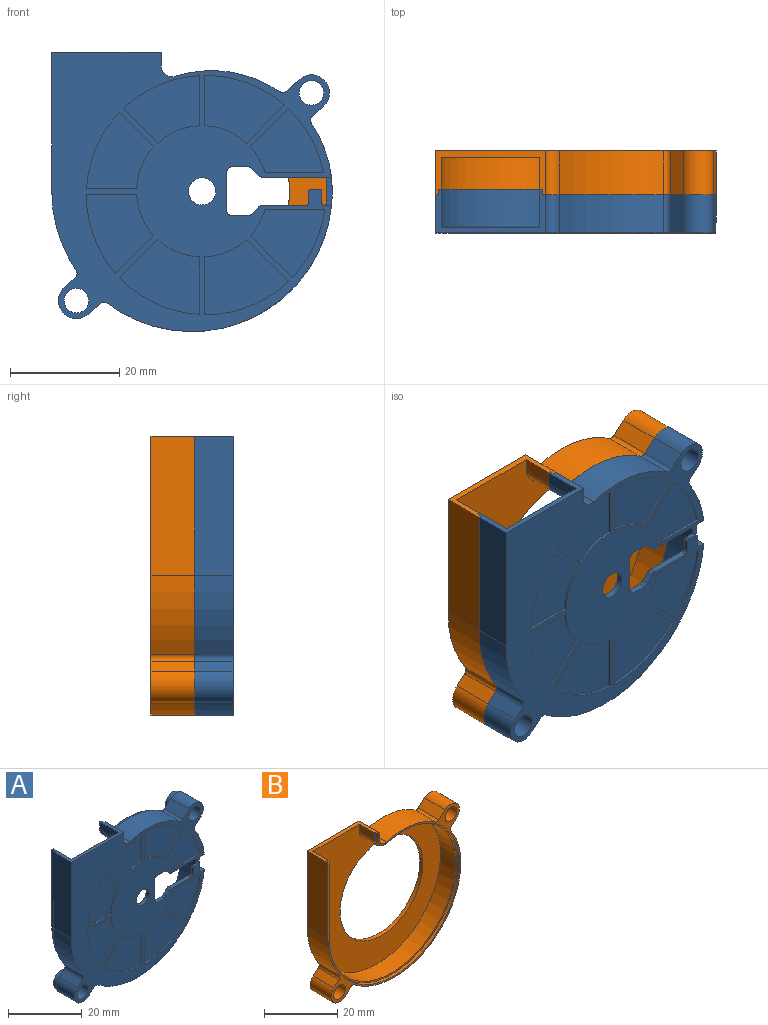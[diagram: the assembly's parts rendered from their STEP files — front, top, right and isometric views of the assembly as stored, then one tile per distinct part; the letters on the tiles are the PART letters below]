
ASSEMBLY  parts=2 mates=1
PART A: 104 faces, bbox 52.9x8.5x51.4 mm
  f0: torus R=1.41mm, axis (0,-1,0), area 1.6mm2, adj f31,f35,f102,f103
  f1: cylinder r=21.88mm len=15.3mm, axis (0,-1,0), area 8.4mm2, adj f14,f53,f54,f55
  f2: cylinder r=2.82mm len=5.65mm, axis (0,-1,0), area 26.6mm2, adj f15,f41
  f3: cylinder r=2.82mm len=5.65mm, axis (0,-1,0), area 26.6mm2, adj f15,f40
  f4: cylinder r=21.57mm len=28.05mm, axis (0,1,0), area 40.5mm2, adj f15,f16,f37,f38
  f5: cylinder r=21.07mm len=27.4mm, axis (0,1,0), area 266.7mm2, adj f16,f31,f33,f34,f86,f87
  f6: cylinder r=2.5mm len=5mm, axis (0,-1,0), area 18.8mm2, adj f14,f31
  f7: cylinder r=2.25mm len=8.5mm, axis (0,-1,0), area 120.2mm2, adj f14,f40
  f8: cylinder r=2.25mm len=8.5mm, axis (0,-1,0), area 120.2mm2, adj f14,f41
  f9: cylinder r=25.65mm len=41.13mm, axis (0,-1,0), area 393.3mm2, adj f13,f14,f15,f28,f29,f87
  f10: cylinder r=1mm len=7mm, axis (0,-1,0), area 9.3mm2, adj f14,f15,f23,f24
  f11: cylinder r=2mm len=7mm, axis (0,-1,0), area 26.3mm2, adj f14,f15,f22,f23
  f12: cylinder r=3.3mm len=7mm, axis (0,-1,0), area 72.6mm2, adj f14,f15,f17,f30
  f13: plane 12.66x2mm, normal (0,0,1), area 13.2mm2, adj f9,f14,f31,f34,f87,f93,f95,f98
  f14: plane 51.17x51.07mm, normal (0,-1,0), area 1131.7mm2, adj f1,f6,f7,f8,f9,f10,f11,f12
  f15: plane 51.3x51.07mm, normal (0,1,0), area 108.5mm2, adj f2,f3,f4,f9,f10,f11,f12,f17
  f16: plane 50.57x50.3mm, normal (0,1,0), area 75.6mm2, adj f4,f5,f21,f32,f33,f34,f35,f36
  f17: plane 7x1.98mm, normal (-0.66,0,0.75), area 18.5mm2, adj f12,f14,f15,f18
  f18: cylinder r=1mm len=7mm, axis (0,-1,0), area 10.1mm2, adj f14,f15,f17,f19
  f19: cylinder r=25.65mm len=14.47mm, axis (0,-1,0), area 107.6mm2, adj f14,f15,f18,f20
  f20: plane 25.4x7mm, normal (-1,0,0), area 177.8mm2, adj f14,f15,f19,f21
  f21: plane 20x8mm, normal (0,0,1), area 31.2mm2, adj f14,f15,f16,f20,f22,f32,f35,f36
  f22: plane 7x2.44mm, normal (1,0,0), area 17.1mm2, adj f11,f14,f15,f21
  f23: cylinder r=22.07mm len=19.05mm, axis (0,-1,0), area 139.5mm2, adj f10,f11,f14,f15
  f24: plane 7x2.44mm, normal (-0.66,0,0.75), area 22.8mm2, adj f10,f14,f15,f25
  f25: cylinder r=3.3mm len=7mm, axis (0,-1,0), area 72.6mm2, adj f14,f15,f24,f26
  f26: plane 7x2.04mm, normal (0.66,0,-0.75), area 19.1mm2, adj f14,f15,f25,f27
  f27: cylinder r=1mm len=7mm, axis (0,-1,0), area 10.1mm2, adj f14,f15,f26,f28
  f28: cylinder r=22.07mm len=12.41mm, axis (0,-1,0), area 87.1mm2, adj f9,f14,f15,f27,f86,f87
  f29: cylinder r=1mm len=7mm, axis (0,-1,0), area 9.6mm2, adj f9,f14,f15,f30
  f30: plane 7x2.22mm, normal (0.66,0,-0.75), area 20.7mm2, adj f12,f14,f15,f29
  f31: plane 49.16x46.35mm, normal (0,1,0), area 1650.7mm2, adj f0,f5,f6,f13,f33,f34,f35,f81
  f32: plane 7.1x2.44mm, normal (-1,0,0), area 17.4mm2, adj f16,f21,f33,f102
  f33: cylinder r=3mm len=7.1mm, axis (0,1,0), area 38.5mm2, adj f5,f16,f31,f32,f103
  f34: cylinder r=24.65mm len=49.3mm, axis (0,1,0), area 524.7mm2, adj f5,f13,f16,f31,f35,f87
  f35: plane 25.4x7.1mm, normal (1,0,0), area 179.6mm2, adj f0,f16,f21,f31,f34,f102
  f36: plane 25.4x1mm, normal (-1,0,0), area 25.4mm2, adj f15,f16,f21,f37
  f37: cylinder r=25.15mm len=50.3mm, axis (0,1,0), area 79mm2, adj f4,f15,f16,f36
  f38: cylinder r=2.5mm len=3.25mm, axis (0,1,0), area 4.7mm2, adj f4,f15,f16,f39
  f39: plane 2.44x1mm, normal (1,0,0), area 2.4mm2, adj f15,f16,f21,f38
  f40: plane 5.65x5.65mm, normal (0,1,0), area 9.2mm2, adj f3,f7
  f41: plane 5.65x5.65mm, normal (0,1,0), area 9.2mm2, adj f2,f8
  f42: plane 6.99x6.99mm, normal (0.71,0,-0.71), area 4.9mm2, adj f14,f43,f45,f46
  f43: cylinder r=12mm len=7.62mm, axis (0,-1,0), area 4.2mm2, adj f14,f42,f44,f46
  f44: plane 10.54x0.5mm, normal (-1,0,0), area 5.3mm2, adj f14,f43,f45,f46
  f45: cylinder r=21.88mm len=14.61mm, axis (0,-1,0), area 8.2mm2, adj f14,f42,f44,f46
  f46: plane 14.61x13.7mm, normal (0,-1,0), area 127.2mm2, adj f42,f43,f44,f45
  f47: plane 7.67x7.67mm, normal (0.71,0,0.71), area 5.4mm2, adj f14,f48,f50,f51
  f48: cylinder r=12mm len=4.77mm, axis (0,-1,0), area 2.8mm2, adj f14,f47,f49,f51
  f49: plane 10.88x0.5mm, normal (0,0,-1), area 5.4mm2, adj f14,f48,f50,f51
  f50: cylinder r=21.88mm len=12.45mm, axis (0,-1,0), area 7mm2, adj f14,f47,f49,f51
  f51: plane 13.57x12.45mm, normal (0,-1,0), area 105.4mm2, adj f47,f48,f49,f50
  f52: cylinder r=12mm len=7.62mm, axis (0,-1,0), area 4.2mm2, adj f14,f53,f54,f55
  f53: plane 7.67x7.67mm, normal (-0.71,0,-0.71), area 5.4mm2, adj f1,f14,f52,f55
  f54: plane 10.57x0.5mm, normal (1,0,0), area 5.3mm2, adj f1,f14,f52,f55
  f55: plane 15.3x13.73mm, normal (0,-1,0), area 135.9mm2, adj f1,f52,f53,f54
  f56: cylinder r=12mm len=7.62mm, axis (0,-1,0), area 4.2mm2, adj f14,f57,f59,f60
  f57: plane 9.2x0.5mm, normal (1,0,0), area 4.6mm2, adj f14,f56,f58,f60
  f58: cylinder r=21.88mm len=14.58mm, axis (0,-1,0), area 7.9mm2, adj f14,f57,f59,f60
  f59: plane 6.96x6.96mm, normal (-0.71,0,0.71), area 4.9mm2, adj f14,f56,f58,f60
  f60: plane 14.58x12.36mm, normal (0,-1,0), area 115.4mm2, adj f56,f57,f58,f59
  f61: cylinder r=12mm len=4.77mm, axis (0,-1,0), area 2.8mm2, adj f14,f62,f64,f65
  f62: plane 6.99x6.99mm, normal (0.71,0,-0.71), area 4.9mm2, adj f14,f61,f63,f65
  f63: cylinder r=21.88mm len=11.76mm, axis (0,-1,0), area 6.8mm2, adj f14,f62,f64,f65
  f64: plane 10.66x0.5mm, normal (0,0,1), area 5.3mm2, adj f14,f61,f63,f65
  f65: plane 13.36x11.76mm, normal (0,-1,0), area 97mm2, adj f61,f62,f63,f64
  f66: cylinder r=12mm len=7.62mm, axis (0,-1,0), area 4.2mm2, adj f14,f67,f69,f70
  f67: plane 9.17x0.5mm, normal (0,0,1), area 4.6mm2, adj f14,f66,f68,f70
  f68: cylinder r=21.88mm len=13.93mm, axis (0,-1,0), area 7.7mm2, adj f14,f67,f69,f70
  f69: plane 6.3x6.3mm, normal (-0.71,0,-0.71), area 4.5mm2, adj f14,f66,f68,f70
  f70: plane 13.93x12.33mm, normal (0,-1,0), area 107.6mm2, adj f66,f67,f68,f69
  f71: plane 9.17x0.5mm, normal (-1,0,0), area 4.6mm2, adj f14,f72,f74,f75
  f72: cylinder r=12mm len=7.62mm, axis (0,-1,0), area 4.2mm2, adj f14,f71,f73,f75
  f73: plane 6.3x6.3mm, normal (0.71,0,0.71), area 4.5mm2, adj f14,f72,f74,f75
  f74: cylinder r=21.88mm len=13.93mm, axis (0,-1,0), area 7.7mm2, adj f14,f71,f73,f75
  f75: plane 13.93x12.33mm, normal (0,-1,0), area 107.6mm2, adj f71,f72,f73,f74
  f76: cylinder r=12mm len=7.62mm, axis (0,-1,0), area 4.2mm2, adj f14,f77,f79,f80
  f77: plane 6.96x6.96mm, normal (-0.71,0,0.71), area 4.9mm2, adj f14,f76,f78,f80
  f78: cylinder r=21.88mm len=14.58mm, axis (0,-1,0), area 7.9mm2, adj f14,f77,f79,f80
  f79: plane 9.2x0.5mm, normal (0,0,-1), area 4.6mm2, adj f14,f76,f78,f80
  f80: plane 14.58x12.36mm, normal (0,-1,0), area 115.4mm2, adj f76,f77,f78,f79
  f81: plane 1.31x1.31mm, normal (-0.71,0,0.71), area 2.2mm2, adj f14,f31,f92,f93
  f82: plane 2.79x1.2mm, normal (0,0,1), area 3.3mm2, adj f14,f31,f91,f92
  f83: plane 7x1.2mm, normal (1,0,0), area 8.4mm2, adj f14,f31,f88,f91
  f84: plane 2.79x1.2mm, normal (0,0,-1), area 3.3mm2, adj f14,f31,f88,f90
  f85: plane 1.31x1.31mm, normal (-0.71,0,-0.71), area 2.2mm2, adj f14,f31,f89,f90
  f86: plane 12.63x2mm, normal (0,0,-1), area 16mm2, adj f5,f14,f28,f31,f87,f89
  f87: plane 5.2x1.16mm, normal (0,-1,0), area 5.2mm2, adj f5,f9,f13,f28,f34,f86
  f88: cylinder r=1mm len=1.2mm, axis (0,1,0), area 1.9mm2, adj f14,f31,f83,f84
  f89: cylinder r=1mm len=1.2mm, axis (0,-1,0), area 0.9mm2, adj f14,f31,f85,f86
  f90: cylinder r=1mm len=1.2mm, axis (0,1,0), area 0.9mm2, adj f14,f31,f84,f85
  f91: cylinder r=1mm len=1.2mm, axis (0,1,0), area 1.9mm2, adj f14,f31,f82,f83
  f92: cylinder r=1mm len=1.2mm, axis (0,1,0), area 0.9mm2, adj f14,f31,f81,f82
  f93: cylinder r=1mm len=1.2mm, axis (0,-1,0), area 0.9mm2, adj f13,f14,f31,f81
  f94: plane 2x0.8mm, normal (1,0,0), area 1.6mm2, adj f14,f95,f100,f101
  f95: plane 3.5x3mm, normal (0,1,0), area 7.5mm2, adj f13,f94,f96,f97,f98,f99,f100,f101
  f96: plane 2x0.8mm, normal (-1,0,0), area 1.6mm2, adj f14,f95,f98,f99
  f97: plane 1.5x0.8mm, normal (0,0,1), area 1.2mm2, adj f14,f95,f99,f100
  f98: cylinder r=0.5mm len=0.8mm, axis (0,1,0), area 0.6mm2, adj f13,f14,f95,f96
  f99: cylinder r=0.5mm len=0.8mm, axis (0,1,0), area 0.6mm2, adj f14,f95,f96,f97
  f100: cylinder r=0.5mm len=0.8mm, axis (0,-1,0), area 0.6mm2, adj f14,f94,f95,f97
  f101: cylinder r=0.5mm len=0.8mm, axis (0,-1,0), area 0.6mm2, adj f13,f14,f94,f95
  f102: plane 22.44x18mm, normal (0,1,0), area 150.3mm2, adj f0,f21,f32,f35,f103
  f103: torus R=22.35mm, axis (0,1,0), area 37.3mm2, adj f0,f31,f33,f102
PART B: 35 faces, bbox 51.3x8x51.1 mm
  f0: cylinder r=25.15mm len=50.3mm, axis (0,-1,0), area 79mm2, adj f28,f32,f33,f34
  f1: cylinder r=2.5mm len=3.25mm, axis (0,-1,0), area 4.7mm2, adj f28,f31,f32,f34
  f2: cylinder r=2.25mm len=8mm, axis (0,1,0), area 113.1mm2, adj f28,f29
  f3: cylinder r=2.25mm len=8mm, axis (0,1,0), area 113.1mm2, adj f28,f29
  f4: cylinder r=22.07mm len=19.05mm, axis (0,1,0), area 159.4mm2, adj f20,f21,f28,f29
  f5: cylinder r=3.3mm len=8mm, axis (0,1,0), area 82.9mm2, adj f18,f19,f28,f29
  f6: cylinder r=1mm len=8mm, axis (0,1,0), area 11mm2, adj f14,f15,f28,f29
  f7: cylinder r=16mm len=32mm, axis (0,1,0), area 120.6mm2, adj f29,f30
  f8: cylinder r=24.65mm len=49.3mm, axis (0,-1,0), area 449.3mm2, adj f11,f12,f30,f34
  f9: cylinder r=3mm len=5.8mm, axis (0,-1,0), area 32.6mm2, adj f10,f11,f30,f34
  f10: plane 5.8x2.44mm, normal (-1,0,0), area 14.2mm2, adj f9,f23,f30,f34
  f11: cylinder r=21.07mm len=27.4mm, axis (0,-1,0), area 229.2mm2, adj f8,f9,f30,f34
  f12: plane 25.4x5.8mm, normal (1,0,0), area 147.3mm2, adj f8,f23,f30,f34
  f13: cylinder r=3.3mm len=8mm, axis (0,1,0), area 82.9mm2, adj f14,f27,f28,f29
  f14: plane 8x2.22mm, normal (0.66,0,-0.75), area 23.7mm2, adj f6,f13,f28,f29
  f15: cylinder r=25.65mm len=41.13mm, axis (0,1,0), area 455.4mm2, adj f6,f16,f28,f29
  f16: cylinder r=22.07mm len=12.41mm, axis (0,1,0), area 105.5mm2, adj f15,f17,f28,f29
  f17: cylinder r=1mm len=8mm, axis (0,1,0), area 11.6mm2, adj f16,f18,f28,f29
  f18: plane 8x2.04mm, normal (0.66,0,-0.75), area 21.8mm2, adj f5,f17,f28,f29
  f19: plane 8x2.44mm, normal (-0.66,0,0.75), area 26mm2, adj f5,f20,f28,f29
  f20: cylinder r=1mm len=8mm, axis (0,1,0), area 10.6mm2, adj f4,f19,f28,f29
  f21: cylinder r=2mm len=8mm, axis (0,1,0), area 30mm2, adj f4,f22,f28,f29
  f22: plane 8x2.44mm, normal (1,0,0), area 19.6mm2, adj f21,f23,f28,f29
  f23: plane 20x8mm, normal (0,0,1), area 36.6mm2, adj f10,f12,f22,f24,f28,f29,f30,f31
  f24: plane 25.4x8mm, normal (-1,0,0), area 203.2mm2, adj f23,f25,f28,f29
  f25: cylinder r=25.65mm len=14.47mm, axis (0,1,0), area 122.9mm2, adj f24,f26,f28,f29
  f26: cylinder r=1mm len=8mm, axis (0,1,0), area 11.6mm2, adj f25,f27,f28,f29
  f27: plane 8x1.98mm, normal (-0.66,0,0.75), area 21.1mm2, adj f13,f26,f28,f29
  f28: plane 51.3x51.07mm, normal (0,-1,0), area 126.8mm2, adj f0,f1,f2,f3,f4,f5,f6,f13
  f29: plane 51.3x51.07mm, normal (0,1,0), area 1370.5mm2, adj f2,f3,f4,f5,f6,f7,f13,f14
  f30: plane 50.07x49.3mm, normal (0,-1,0), area 1168mm2, adj f7,f8,f9,f10,f11,f12,f23
  f31: plane 2.44x1mm, normal (-1,0,0), area 2.4mm2, adj f1,f23,f28,f34
  f32: cylinder r=21.57mm len=28.05mm, axis (0,-1,0), area 40.5mm2, adj f0,f1,f28,f34
  f33: plane 25.4x1mm, normal (1,0,0), area 25.4mm2, adj f0,f23,f28,f34
  f34: plane 50.57x50.3mm, normal (0,-1,0), area 75.6mm2, adj f0,f1,f8,f9,f10,f11,f12,f23
PLACE A t=(-11.79,-5.71,-0.35)mm fixed
PLACE B t=(-11.79,9.29,-0.35)mm
MATE fastened B.f3 <-> A.f2  axis (0,-1,0) through (-34.79,1.29,-20.35)mm
